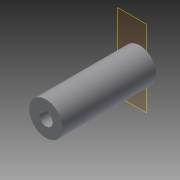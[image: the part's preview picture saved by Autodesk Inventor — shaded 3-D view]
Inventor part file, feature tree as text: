
AUTODESK INVENTOR PART (.ipt)
format: ipt  version: 2015 (Build 190159000, 159)  size: 77,312 bytes
history: native  units: in
note: dims shown in document units (in); Inventor stores cm internally (conversion verified against a paired STEP export)
features: plane x3, extrude x1, sketch x1, reference x1
ambient origin geometry x8: Origin, YZ Plane, XZ Plane, XY Plane, X Axis, Y Axis, Z Axis, Center Point
bodies: Solid1 (feature_tree)
feature tree (6):
  plane  "Work Plane1"
  plane  "Work Plane2"
  plane  "Work Plane3"
  extrude  "Extrusion1"  [1 undecoded]
  sketch  "Sketch1"  dims[d0=1.3226in d1=0.0in]
  reference  "Reference1"
note: 1 required parameter value undecoded (feature->parameter linkage not recoverable at this tier; creation-order binding heuristic only, values carry confidence <= 0.55)
